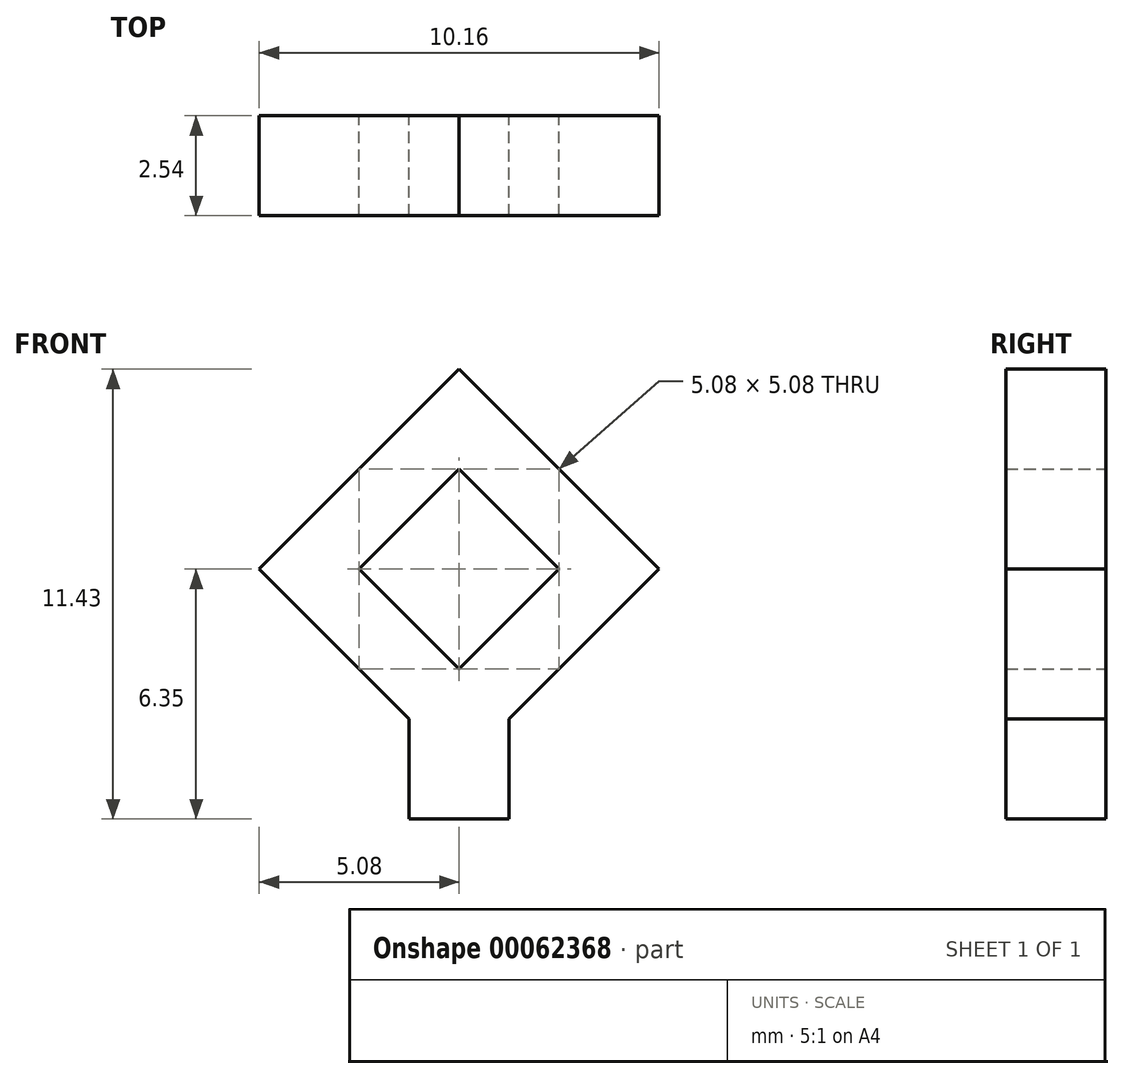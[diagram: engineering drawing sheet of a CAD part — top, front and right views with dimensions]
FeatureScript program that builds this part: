
annotation { "Feature Type Name" : "Feature", "Feature Type Description" : "" }
export const myFeature = defineFeature(function(context is Context, id is Id, definition is map)
    precondition{}
    {
        {
            var Q0;
            Q0=qCreatedBy(makeId("Front.planeOp"),FACE);
            var sketch = newSketch(context, id + "F0", { "sketchPlane" : qUnion([Q0])});
            skLineSegment(sketch, "E0", {"start": v(0, 0) * mm, "end": v(0, 3.81) * mm});
            skLineSegment(sketch, "E1", {"start": v(0, 3.81) * mm, "end": v(-2.54, 6.35) * mm});
            skLineSegment(sketch, "E2", {"start": v(-2.54, 6.35) * mm, "end": v(0, 8.9) * mm});
            skLineSegment(sketch, "E3", {"start": v(0, 8.9) * mm, "end": v(2.54, 6.35) * mm});
            skLineSegment(sketch, "E4", {"start": v(2.54, 6.35) * mm, "end": v(0, 3.8) * mm});
            skLineSegment(sketch, "E5", {"start": v(0, 0) * mm, "end": v(1.27, 0) * mm});
            skLineSegment(sketch, "E6", {"start": v(1.27, 0) * mm, "end": v(1.27, 2.54) * mm});
            skLineSegment(sketch, "E7", {"start": v(1.27, 2.54) * mm, "end": v(5.08, 6.35) * mm});
            skLineSegment(sketch, "E8", {"start": v(5.08, 6.35) * mm, "end": v(0, 11.43) * mm});
            skLineSegment(sketch, "E9", {"start": v(0, 11.43) * mm, "end": v(-5.08, 6.35) * mm});
            skLineSegment(sketch, "E10", {"start": v(-5.08, 6.35) * mm, "end": v(-1.27, 2.54) * mm});
            skLineSegment(sketch, "E11", {"start": v(-1.27, 2.54) * mm, "end": v(-1.27, 0) * mm});
            skLineSegment(sketch, "E12", {"start": v(-1.27, 0) * mm, "end": v(0, 0) * mm});
            skLineSegment(sketch, "E13", {"start": v(0, 3.81) * mm, "end": v(1.27, 2.54) * mm, "construction": true});
            skLineSegment(sketch, "E14", {"start": v(-1.27, 2.54) * mm, "end": v(0, 3.81) * mm, "construction": true});
            skLineSegment(sketch, "E15", {"start": v(-2.54, 6.35) * mm, "end": v(-5.08, 6.35) * mm, "construction": true});
            skLineSegment(sketch, "E16", {"start": v(0, 8.9) * mm, "end": v(0, 11.43) * mm, "construction": true});
            skLineSegment(sketch, "E17", {"start": v(2.54, 6.35) * mm, "end": v(5.08, 6.35) * mm, "construction": true});
            skSolve(sketch);
        }
        {
            var Q0;
            Q0=makeQuery(id+"F0.imprint","IMPRINT",FACE,{"disambiguationData":[TD([[makeQuery(id+"F0.imprint","IMPRINT",EDGE,{"derivedFrom":sQuery(id+"F0.wireOp",EDGE,"E1")}),1.0]])]});
            extrude(context, id + "F1", {"entities" : qUnion([Q0]), "depth" : 2.54 * mm});
        }
    });
